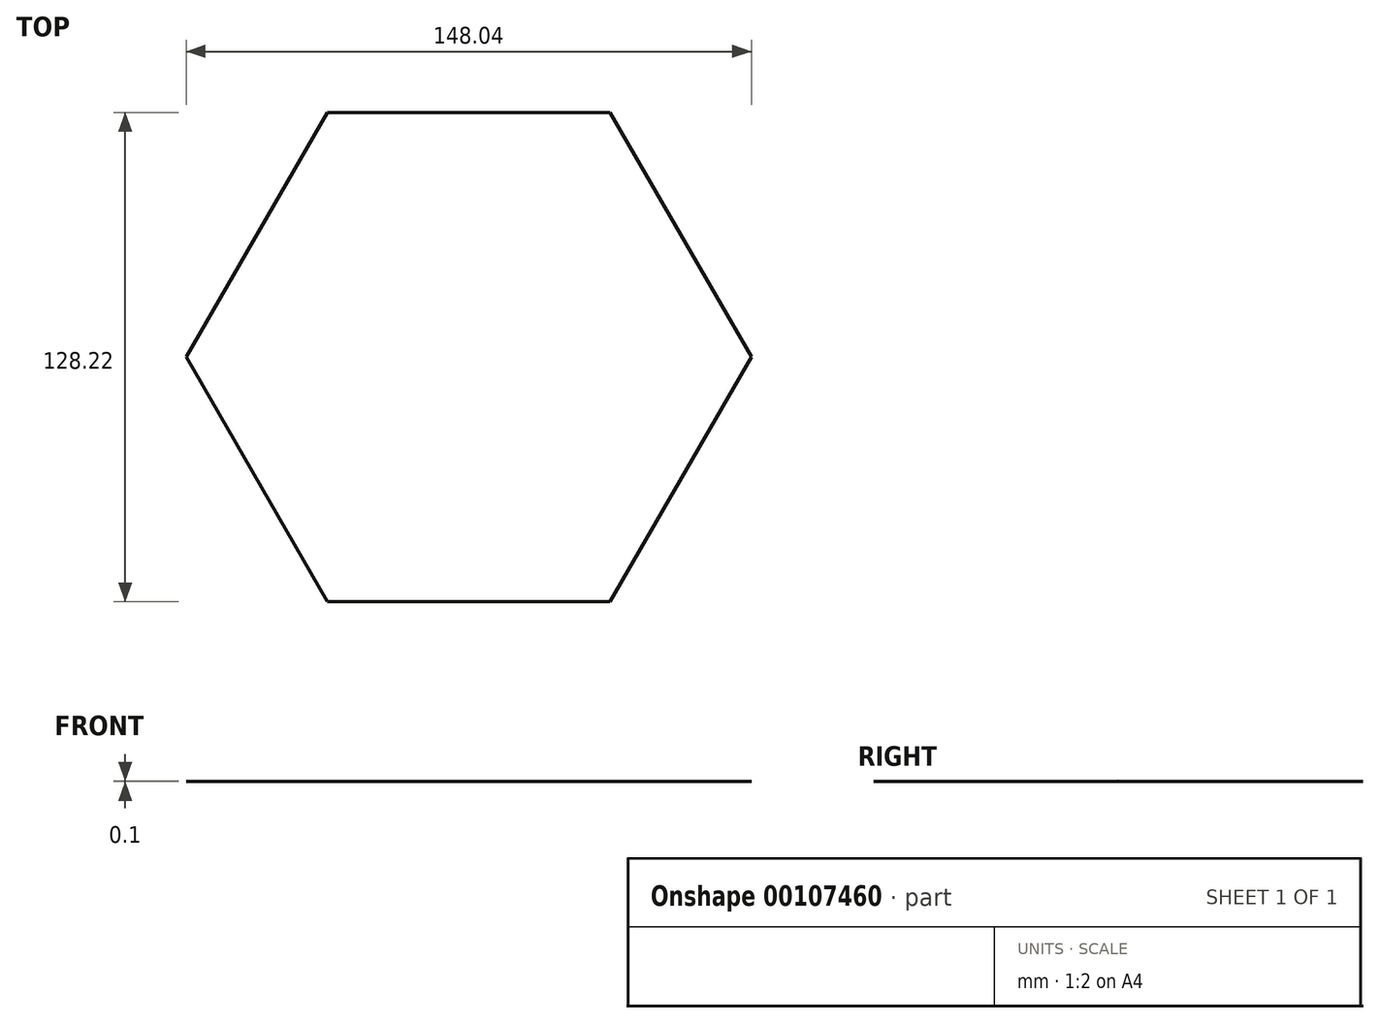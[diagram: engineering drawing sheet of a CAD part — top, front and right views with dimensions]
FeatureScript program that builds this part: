
annotation { "Feature Type Name" : "Feature", "Feature Type Description" : "" }
export const myFeature = defineFeature(function(context is Context, id is Id, definition is map)
    precondition{}
    {
        {
            var Q0;
            Q0=qCreatedBy(makeId("Top.planeOp"),FACE);
            var sketch = newSketch(context, id + "F0", { "sketchPlane" : qUnion([Q0])});
            skCircle(sketch, "E0.cCircle", {"center": v(0, 0) * mm, "radius": 64.1 * mm, "construction": true});
            skLineSegment(sketch, "E0.0", {"start": v(-74.02, 0) * mm, "end": v(-37.01, 64.1) * mm});
            skLineSegment(sketch, "E0.1", {"start": v(-37.01, 64.1) * mm, "end": v(37.01, 64.1) * mm});
            skLineSegment(sketch, "E0.2", {"start": v(37.01, 64.1) * mm, "end": v(74.02, 0) * mm});
            skLineSegment(sketch, "E0.3", {"start": v(74.02, 0) * mm, "end": v(37.01, -64.1) * mm});
            skLineSegment(sketch, "E0.4", {"start": v(37.01, -64.1) * mm, "end": v(-37.01, -64.1) * mm});
            skLineSegment(sketch, "E0.5", {"start": v(-37.01, -64.1) * mm, "end": v(-74.02, 0) * mm});
            skPoint(sketch, "E0.0.midPoint", {"position": v(-55.52, 32.05) * mm});
            skSolve(sketch);
        }
        {
            var Q0;
            Q0=qCreatedBy(makeId("Top.planeOp"),FACE);
            cPlane(context, id + "F1", {"entities" : qUnion([Q0]), "cplaneType" : CPlaneType.OFFSET, "offset" : .1 * mm, "width" : 150 * mm, "height" : 150 * mm});
        }
        {
            var Q0;
            Q0=qCreatedBy(id+"F1.planeOp",FACE);
            var sketch = newSketch(context, id + "F2", { "sketchPlane" : qUnion([Q0])});
            skPoint(sketch, "E1", {"position": v(0, 0) * mm});
            skSolve(sketch);
        }
        {
            var Q0;
            Q0=sQuery(id+"F2.wireOp",VERTEX,"E1");
            var Q1;
            Q1=qConstructionFilter(qBodyType(qCreatedBy(id+"F0",EDGE),BodyType.WIRE),ConstructionObject.NO);
            loft(context, id + "F3", {"bodyType" : ToolBodyType.SURFACE, "wireProfilesArray" : [{ "wireProfileEntities" : qUnion([Q0]) }, { "wireProfileEntities" : qUnion([Q1]) }]});
        }
    });
